# Revit family: Domotics-DomesticRanges-GEWISS-27COMBI_SYSTEM-IP55_INDICATOR_LAMPS
name_source: partatom
category: Modelli generici
revit_build: Autodesk Revit 2016 (Build: 20161004_0715(x64)
units: mm (PartAtom-declared; Revit-internal decimal feet)

## family parameters
Condiviso = No
Host = Muro
Punto di calcolo locali = No
Può ospitare armatura = No
Quota connettore circolare = Usa diametro
Sempre verticale = Sì
Taglio con vuoti quando caricato = No
Tipo di parte = Normale

## types (5) — shared parameters
Catalogue = DOMOTICS
Catalogue Range = 27COMBI
Colore diffusore = GEWISS VETRINO AZZURRO
Colour = Grey RAL 7035
Electrocod = 0132
Glow Wire Test = 650°C
IDF = 3d05019a-1903-455a-b8c8-52a1bfdd14c6
IDT = 7b0adaca-5341-4719-835f-f8f4d184b5d8
IP degree = IP55
Immagine tipo = GW27419.jpg
Installation temperature = -25 +60 °C
Insulation class = II
Lampholder type = E14
Outer dim. LxHxD (mm) = 66x82x95
Power = Max 15W
Produttore = GEWISS S.p.A.
Rated voltage = 230V ac
Standard = EN 60598-1
Technical sheet = https://www.gewiss.com
Thermo-pressure with ball = 70
URL = https://www.gewiss.com
Version file RFA = 18.0

## per-type parameters (varying)
| type | Descrizione | Diffuser colour | EAN code | Modello |
| GW27417 - Yellow watertight diffuser lamp | YELLOW WATERTIGHT DIFFUSER LAMP | Yellow | 8011564056190 | GW27417 |
| GW27416 - Green watertight diffuser lamp | GREEN WATERTIGHT DIFFUSER LAMP | Green | 8011564056183 | GW27416 |
| GW27419 - Blu watertight diffuser lamp | BLU WATERTIGHT DIFFUSER LAMP | Light blue | 8011564056213 | GW27419 |
| GW27415 - Red watertight rcd diffuser lamp | RED WATERTIGHT RCD DIFFUSER LAMP | Red | 8011564056176 | GW27415 |
| GW27418 - Transparent watertight diffuser lamp | TRANSPARENT WATERTIGHT DIFFUSER LAMP | Transparent | 8011564056206 | GW27418 |

note: source unit labels omitted for Thermo-pressure with ball — the stored unit's dimension contradicts the parameter name (converter mislabeling)
